# Revit family: IS_iLifeS_T4594_BIM_GB
name_source: partatom
category: Plumbing Fixtures
units: mm (PartAtom-declared; Revit-internal decimal feet)

## family parameters
Always vertical = No
Cut with Voids When Loaded = No
OmniClass Number = 23.45.05.21.11.11
OmniClass Title = Water Operated Water Closets
Part Type = Normal
Room Calculation Point = No
Round Connector Dimension = Use Diameter
Shared = No
Work Plane-Based = No

## types (1)
- T459401 - i.life S backt-to-wall 48 cm Rim Less WC Bowl Bowl - White
    Accessories = https://www.idealstandard.co.uk
    AreaUnits = millimetres
    AssetType = Fixed
    BIMObjectName = IS_IdealStandard_WC pans_i.lifeS_T4594
    BIMobject category = Toilets
    BIMobject category code = toilets
    BIMobject main category = Sanitary
    BIMobject main category code = sanitary
    BarCode = 8014140491767
    Brand = Ideal Standard
    Brand url = http://www.idealstandard.co.uk
    Category = Sanitary
    Color = White
    ConnectionType = Plumbing
    Cost = 0 $
    CurrencyUnit = £
    CurrentRevision = 1
    Date of publishing = 27/05/2022
    Description = Ideal Standard i.life S backt-to-wall bowl, RimLS+, back-to-wall, L-shape floor fixation, compact 48 cm, white in carton box, EU pallet
    DurationUnit = Years
    Edition number = 1
    ElementType = Fixed
    ExpectedLife = 99
    Features = backt-to-wall bowl, RimLS+, back-to-wall, L-shape floor fixation, compact 48 cm, white in carton box, EU pallet
    Finish = White
    GTIN code = https://8014140491767
    Help = https://www.idealstandard.co.uk
    IFC Classification = Sanitary Terminal
    IfcExportAs = IfcSanitaryTerminalType
    IfcExportType = TOILETPAN
    Installation instructions = https://www.idealstandard.co.uk
    InstallationInstructions = https://www.idealstandard.co.uk
    LinearUnits = Millimetres
    MainColor = White
    MaintenanceInformation = https://www.idealstandard.co.uk
    Manufacturer = Ideal Standard
    Manufacturer name = Ideal Standard
    ManufacturerURL = https://www.idealstandard.co.uk
    Material = Vitrous China
    Material main = Vitrous China
    Model = T459401
    ModelNumber = T459401
    ModelReference = i.life S backt-to-wall 48 cm Rim Less WC Bowl Bowl
    NBS Reference Code = 45-35-70/384
    NBS Reference Description = WC pans
    Name = WC pans_i.lifeS_T4594_IdealStandard
    NettWeight = 23.2
    NominalDepth = 479 mm
    NominalHeight = 400 mm
    NominalLength = 479 mm
    NominalWidth = 353 mm
    OmniClass Code = 23-31 19 00
    OmniClass Description = Toilets
    PanColor = White
    PredefinedType = Sanitary
    Product Guid = 25bc4db2-9a31-46c7-99c8-db0d4706af99
    Product SKU = T4594
    Product certification = https://www.idealstandard.co.uk
    Product data url = https://bimobject.com
    Product family = I.life S
    Product group = Sanitry: WC Pans
    Product name = i.life S backt-to-wall 48 cm Rim Less WC Bowl Bowl
    Product url = https://www.idealstandard.co.uk
    ProductInformation = https://www.idealstandard.co.uk
    QR code = http://bimobject.com
    ReplacementCost = 0
    Shape = Sculpture
    Size = 479 x 400 x 353 mm
    Space = Internal
    SpareParts = https://www.idealstandard.co.uk
    Technical description = https://www.idealstandard.co.uk
    ToiletPanType = back to wall WC Pan
    ToiletType = back to wall WC Pan
    UNSPSC Code = 301815
    URL = https://www.idealstandard.co.uk
    Uniclass 2015 Code = Pr_40_20_93_94
    Uniclass 2015 Name = WC pans
    Uniclass2015Code = Pr_40_20_93_94
    Uniclass2015Title = WC pans
    Uniclass2015Version = v.25
    Version = 1
    VolumeUnits = Litres
    WRASURL = https://www.wrasapprovals.co.uk
    WarrantyDescription = manufacturer warranty
    WarrantyDurationUnit = years
    Youtube clip = https://www.youtube.com

## geometry (parser evidence)
native form markers: Sweep x2
no freeform markers — native parametric forms only
